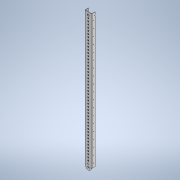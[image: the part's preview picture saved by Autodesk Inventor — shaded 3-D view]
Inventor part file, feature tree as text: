
AUTODESK INVENTOR PART (.ipt)
format: ipt  version: 2022 (Build 260153000, 153)  size: 701,440 bytes
history: native  units: mm
features: sketch x7, extrude x6, sheet_metal_op x3, projected_geometry x3, other x2, pattern_linear x1
ambient origin geometry x8: Origin, YZ Plane, XZ Plane, XY Plane, X Axis, Y Axis, Z Axis, Center Point
bodies: Solid1 (feature_tree)
feature tree (22):
  sheet_metal_op  "Contour Flange1"
  extrude  "Extrusion1"  Depth=50.0mm
  extrude  "Extrusion2"  Depth=1.5mm
  extrude  "Extrusion4"  Depth=0.75mm
  pattern_linear  "Rectangular Pattern1"  Count1=100  [1 undecoded]
  extrude  "Extrusion5"  Depth=1.5mm
  extrude  "Extrusion6"  Depth=1.5mm
  extrude  "Extrusion7"  Depth=1.5mm
  sketch  "Sketch1"  dims[d3=25.0mm d4=50.0mm]
  other  "Plate1"
  sheet_metal_op  "Bend1"
  sheet_metal_op  "Corner1"
  sketch  "Sketch2"  dims[d5=25.0mm d6=1.5mm]
  sketch  "Sketch3"  dims[d7=1.5mm d8=0.75mm]
  projected_geometry  "Projected Loop1"
  projected_geometry  "Projected Loop2"
  sketch  "Sketch5"  dims[d9=3.0mm]
  sketch  "Sketch6"  dims[d10=1.5mm d11=1000.0mm]
  projected_geometry  "Projected Loop5"
  sketch  "Sketch7"  dims[d12=1.5mm d13=1.5mm]
  sketch  "Sketch8"  dims[d14=6.0mm d15=1.5mm d16=1.5mm d17=20.0mm d18=10.0mm d19=25.0mm d20=490.0mm d22=20.0mm d23=10.0mm d25=10.0mm d27=0.0mm d28=0.0mm d29=0.0mm d30=0.0mm d33=3.35mm d34=11.0mm d35=28.0mm d36=0.0mm d37=0.0mm d38=190.0mm d40=50.0mm d41=15.0mm d42=10.0mm d43=0.0mm d44=8.0mm d45=20.0mm d46=0.0mm d47=0.0mm d48=0.25mm d49=0.0mm]
  other  "Definition1"
note: 1 required parameter value undecoded (feature->parameter linkage not recoverable at this tier; creation-order binding heuristic only, values carry confidence <= 0.55)
